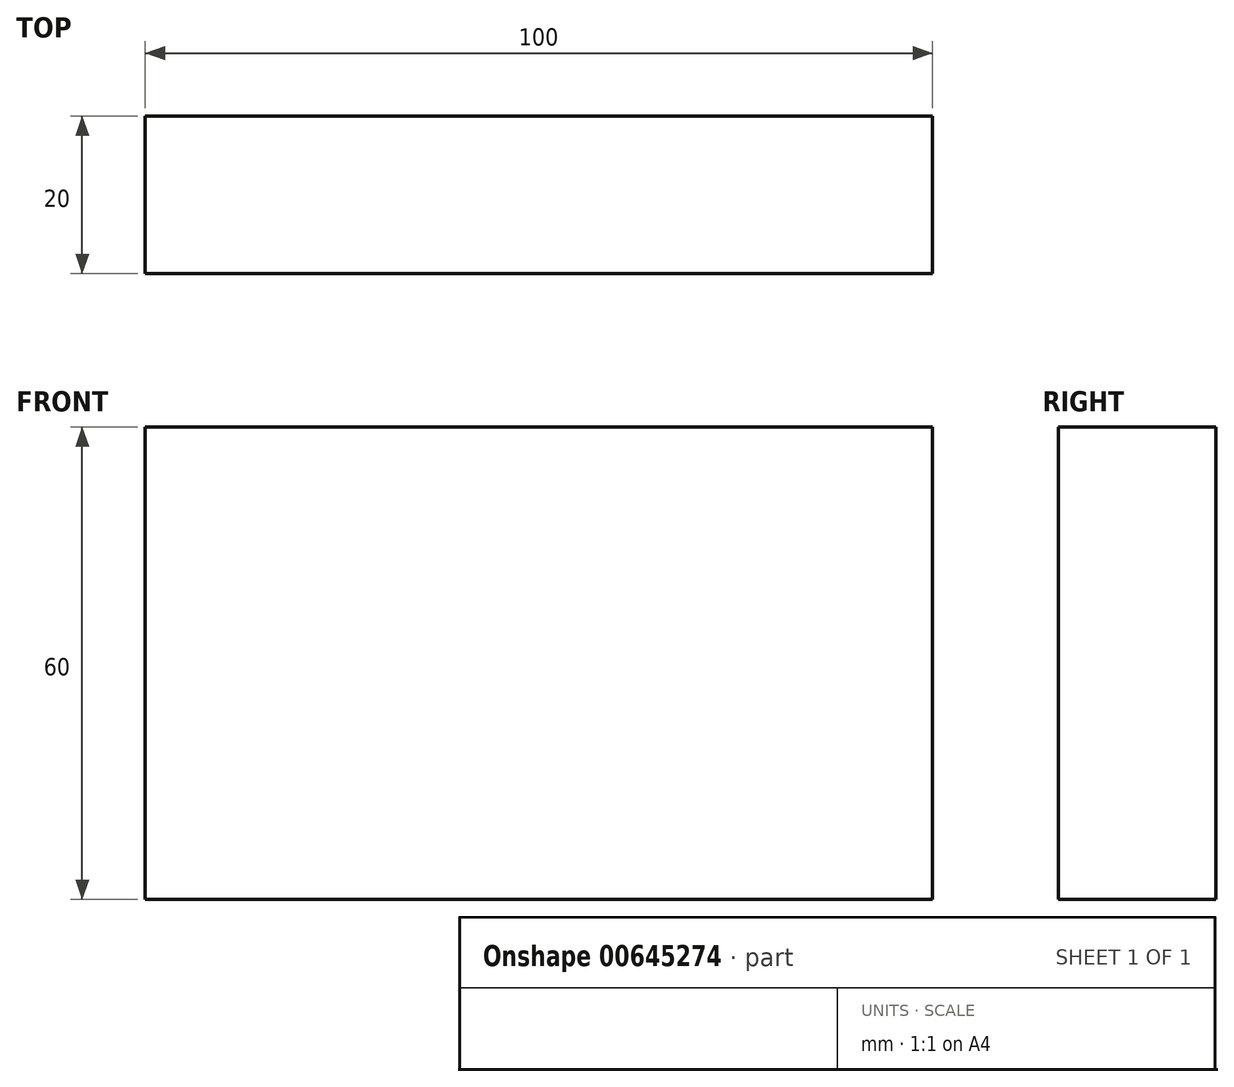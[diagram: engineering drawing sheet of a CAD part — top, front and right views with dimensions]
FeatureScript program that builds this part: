
annotation { "Feature Type Name" : "Feature", "Feature Type Description" : "" }
export const myFeature = defineFeature(function(context is Context, id is Id, definition is map)
    precondition{}
    {
        {
            var Q0;
            Q0=qCreatedBy(makeId("Front.planeOp"),FACE);
            var sketch = newSketch(context, id + "F0", { "sketchPlane" : qUnion([Q0])});
            skLineSegment(sketch, "E0.bottom", {"start": v(-48.85, 25.28) * mm, "end": v(51.15, 25.28) * mm});
            skLineSegment(sketch, "E0.top", {"start": v(-48.85, -34.72) * mm, "end": v(51.15, -34.72) * mm});
            skLineSegment(sketch, "E0.left", {"start": v(-48.85, 25.28) * mm, "end": v(-48.85, -34.72) * mm});
            skLineSegment(sketch, "E0.right", {"start": v(51.15, 25.28) * mm, "end": v(51.15, -34.72) * mm});
            skSolve(sketch);
        }
        {
            var Q0;
            Q0 = qSketchRegion(id + "F0", true);
            extrude(context, id + "F1", {"entities" : qUnion([Q0]), "depth" : 20 * mm, "offsetDistance" : 25.4 * mm});
        }
    });
